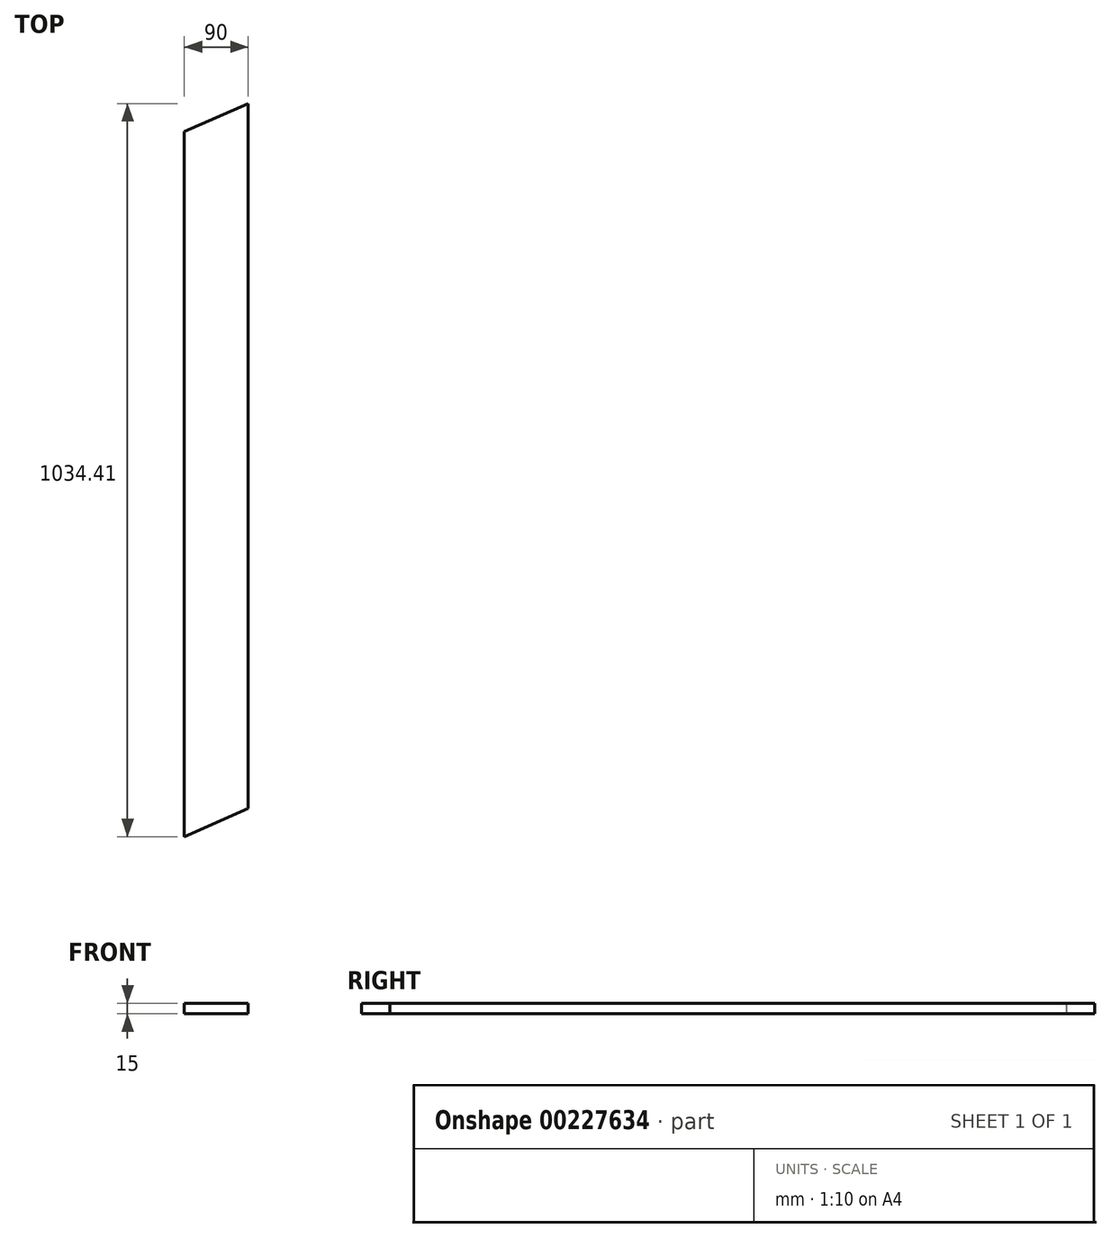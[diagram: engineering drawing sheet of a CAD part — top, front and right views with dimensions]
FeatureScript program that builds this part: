
annotation { "Feature Type Name" : "Feature", "Feature Type Description" : "" }
export const myFeature = defineFeature(function(context is Context, id is Id, definition is map)
    precondition{}
    {
        {
            var Q0;
            Q0=qCreatedBy(makeId("Front.planeOp"),FACE);
            var sketch = newSketch(context, id + "F0", { "sketchPlane" : qUnion([Q0])});
            skLineSegment(sketch, "E0.bottom", {"start": v(-44.13, 2.06) * mm, "end": v(45.87, 2.06) * mm});
            skLineSegment(sketch, "E0.top", {"start": v(-44.13, -12.94) * mm, "end": v(45.87, -12.94) * mm});
            skLineSegment(sketch, "E0.left", {"start": v(-44.13, 2.06) * mm, "end": v(-44.13, -12.94) * mm});
            skLineSegment(sketch, "E0.right", {"start": v(45.87, 2.06) * mm, "end": v(45.87, -12.94) * mm});
            skSolve(sketch);
        }
        {
            var Q0;
            Q0=makeQuery(id+"F0.imprint","IMPRINT",FACE,{"disambiguationData":[TD([[makeQuery(id+"F0.imprint","IMPRINT",EDGE,{"derivedFrom":sQuery(id+"F0.wireOp",EDGE,"E0.bottom")}),-1.0]])]});
            extrude(context, id + "F1", {"entities" : qUnion([Q0]), "oppositeDirection" : true, "depth" : 1034.4 * mm});
        }
        {
            var Q0;
            Q0=makeQuery(id+"F1.opExtrude","SWEPT_FACE",FACE,{"disambiguationData":[OSD([sQuery(id+"F0.wireOp",EDGE,"E0.top")])]});
            var sketch = newSketch(context, id + "F2", { "sketchPlane" : qUnion([Q0])});
            skLineSegment(sketch, "E1", {"start": v(-44.13, 0) * mm, "end": v(45.87, -39.72) * mm});
            skLineSegment(sketch, "E2", {"start": v(45.87, -1034.4) * mm, "end": v(-44.13, -994.69) * mm});
            skSolve(sketch);
        }
        {
            var Q0;
            {var subQ0=sQuery(id+"F2.wireOp",EDGE,"E1");Q0=makeQuery(id+"F2.imprint","IMPRINT",FACE,{"disambiguationData":[TD([[makeQuery(id+"F2.imprint","IMPRINT",EDGE,{"derivedFrom":subQ0}),1.0]])]});}
            var Q1;
            {var subQ0=sQuery(id+"F2.wireOp",EDGE,"E2");Q1=makeQuery(id+"F2.imprint","IMPRINT",FACE,{"disambiguationData":[TD([[makeQuery(id+"F2.imprint","IMPRINT",EDGE,{"derivedFrom":subQ0}),1.0]])]});}
            extrude(context, id + "F3", {"entities" : qUnion([Q0, Q1]), "operationType" : NewBodyOperationType.REMOVE, "oppositeDirection" : true, "depth" : 15 * mm});
        }
    });
